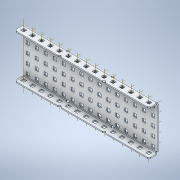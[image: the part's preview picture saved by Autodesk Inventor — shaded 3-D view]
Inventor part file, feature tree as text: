
AUTODESK INVENTOR PART (.ipt)
format: ipt  version: 2020 (Build 240168000, 168)  size: 1,589,760 bytes
history: native  units: in
note: dims shown in document units (in); Inventor stores cm internally (conversion verified against a paired STEP export)
features: other x108, plane x4, pattern_linear x3, split x1, imported_body x1
ambient origin geometry x8: Origin, YZ Plane, XZ Plane, XY Plane, X Axis, Y Axis, Z Axis, Center Point
bodies: Solid1 (feature_tree)
feature tree (117):
  plane  "Work Plane1"
  plane  "Work Plane2"
  plane  "Work Plane3"
  other  "Work Point1"
  other  "Work Point2"
  other  "Work Axis1"
  other  "Work Axis2"
  other  "Work Axis3"
  pattern_linear  "Rectangular Pattern1"  Count1=15 Spacing1=0.5in
  pattern_linear  "Rectangular Pattern2"  Count1=15 Spacing1=0.5in
  pattern_linear  "Rectangular Pattern3"  Count1=15 Spacing1=0.5in
  plane  "Work Plane4"
  split  "Split1"
  other  "Work Point3"
  other  "Work Axis4"
  other  "Work Axis5"
  other  "Work Axis6"
  other  "Work Axis7"
  other  "Work Axis8"
  other  "Work Axis9"
  other  "Work Axis10"
  other  "Work Axis11"
  other  "Work Axis12"
  other  "Work Axis13"
  other  "Work Axis14"
  other  "Work Axis15"
  other  "Work Axis16"
  other  "Work Axis17"
  other  "Work Axis38"
  other  "Work Axis39"
  other  "Work Axis40"
  other  "Work Axis41"
  other  "Work Axis42"
  other  "Work Axis43"
  other  "Work Axis44"
  other  "Work Axis45"
  other  "Work Axis46"
  other  "Work Axis47"
  other  "Work Axis48"
  other  "Work Axis49"
  other  "Work Axis50"
  other  "Work Axis51"
  other  "Work Axis52"
  other  "Work Axis73"
  other  "Work Axis74"
  other  "Work Axis75"
  other  "Work Axis76"
  other  "Work Axis77"
  other  "Work Axis78"
  other  "Work Axis79"
  other  "Work Axis80"
  other  "Work Axis81"
  other  "Work Axis82"
  other  "Work Axis83"
  other  "Work Axis84"
  other  "Work Axis85"
  other  "Work Axis86"
  other  "Work Axis87"
  other  "Work Axis108"
  other  "Work Axis109"
  other  "Work Axis110"
  other  "Work Axis111"
  other  "Work Axis112"
  other  "Work Axis113"
  other  "Work Axis114"
  other  "Work Axis115"
  other  "Work Axis116"
  other  "Work Axis117"
  other  "Work Axis118"
  other  "Work Axis119"
  other  "Work Axis120"
  other  "Work Axis121"
  other  "Work Axis122"
  other  "Work Axis143"
  other  "Work Axis144"
  other  "Work Axis145"
  other  "Work Axis146"
  other  "Work Axis147"
  other  "Work Axis148"
  other  "Work Axis149"
  other  "Work Axis150"
  other  "Work Axis151"
  other  "Work Axis152"
  other  "Work Axis153"
  other  "Work Axis154"
  other  "Work Axis155"
  other  "Work Axis156"
  other  "Work Axis157"
  other  "Work Axis178"
  other  "Work Axis179"
  other  "Work Axis180"
  other  "Work Axis181"
  other  "Work Axis182"
  other  "Work Axis183"
  other  "Work Axis184"
  other  "Work Axis185"
  other  "Work Axis186"
  other  "Work Axis187"
  other  "Work Axis188"
  other  "Work Axis189"
  other  "Work Axis190"
  other  "Work Axis191"
  other  "Work Axis212"
  other  "Work Axis213"
  other  "Work Axis214"
  other  "Work Axis215"
  other  "Work Axis216"
  other  "Work Axis217"
  other  "Work Axis218"
  other  "Work Axis219"
  other  "Work Axis220"
  other  "Work Axis221"
  other  "Work Axis222"
  other  "Work Axis223"
  other  "Work Axis224"
  other  "Work Axis225"
  imported_body  "Imported1"
